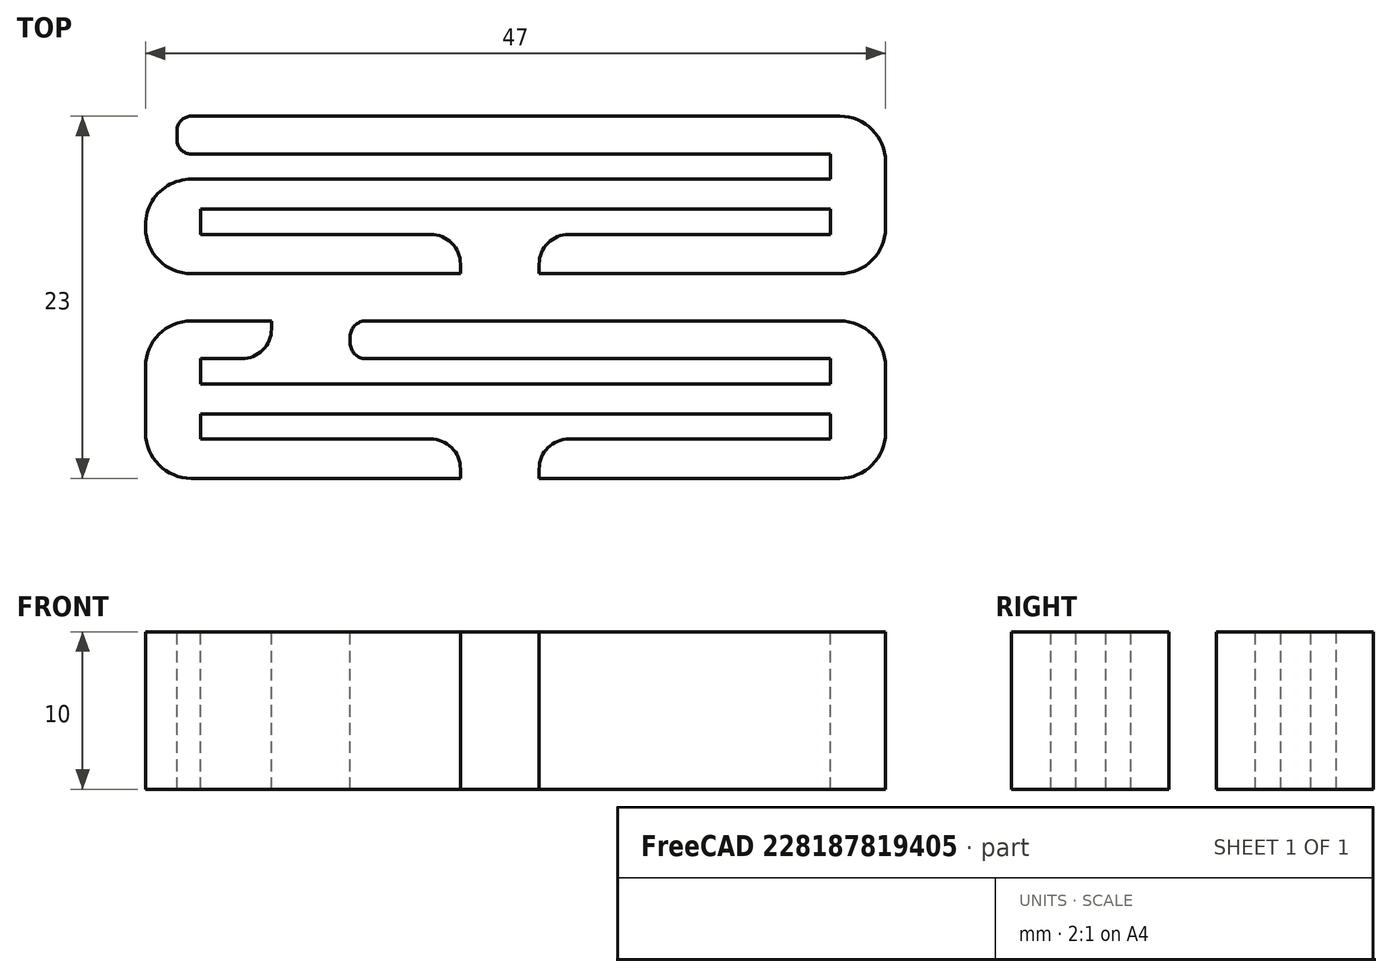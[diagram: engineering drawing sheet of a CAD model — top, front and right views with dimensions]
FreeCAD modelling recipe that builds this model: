
FCSTD DOCUMENT  (FreeCAD 0.16R6706 (Git))
Label: clip_mochila_40mm
License: CC-BY 3.0
LicenseURL: http://creativecommons.org/licenses/by/3.0/
objects: Part::Box×10, Part::Cut×8, Part::Fillet×7
note: 25 computed .brp shape members not serialized (recipe doc carries the construction recipe); baked Part::Feature solids carry a one-line shape summary decoded from their .brp

FEATURE [Part::Box] Box001  label="ext"
  Height = 10
  Length = 47
  Placement = pos=(-2,0,0) rot=(0,0,1;0rad)
  Width = 10
FEATURE [Part::Box] Box002  label="Cubo002"
  Height = 10
  Length = 40
  Placement = pos=(1.5,6,0) rot=(0,0,1;0rad)
  Width = 1.6
FEATURE [Part::Box] Box  label="Cubo003"
  Height = 10
  Length = 40
  Placement = pos=(1.5,2.5,0) rot=(0,0,1;0rad)
  Width = 1.6
FEATURE [Part::Box] Box003  label="Cubo004"
  Height = 10
  Length = 5
  Placement = pos=(18,0,0) rot=(0,0,1;0rad)
  Width = 2.5
FEATURE [Part::Box] Box004  label="Cubo005"
  Height = 10
  Length = 5
  Placement = pos=(6,6,0) rot=(0,0,1;0rad)
  Width = 4
FEATURE [Part::Cut] Cut
  Base = -> Box001
  Tool = -> Box004
FEATURE [Part::Cut] Cut001
  Base = -> Cut
  Tool = -> Box002
FEATURE [Part::Cut] Cut002
  Base = -> Cut001
  Tool = -> Box
FEATURE [Part::Cut] Cut003
  Base = -> Cut002
  Tool = -> Box003
FEATURE [Part::Fillet] Fillet
  Base = -> Cut003
  Edges = 4 edges r=2.9: [Edge1,Edge3,Edge59,Edge60]
FEATURE [Part::Fillet] Fillet001
  Base = -> Fillet
  Edges = 2 edges r=1: [Edge70,Edge72]
FEATURE [Part::Fillet] Fillet002
  Base = -> Fillet001
  Edges = 1 edges r=1.9: [Edge55]
FEATURE [Part::Fillet] Fillet003  label="Pechado"
  Base = -> Fillet002
  Edges = 2 edges r=1.9: [Edge62,Edge82]
FEATURE [Part::Box] Box005  label="ext001"
  Height = 10
  Length = 47
  Placement = pos=(-2,13,0) rot=(0,0,1;0rad)
  Width = 10
FEATURE [Part::Box] Box006  label="Cubo006"
  Height = 10
  Length = 43
  Placement = pos=(-1.5,19,0) rot=(0,0,1;0rad)
  Width = 1.6
FEATURE [Part::Box] Box007  label="Cubo007"
  Height = 10
  Length = 40
  Placement = pos=(1.5,15.5,0) rot=(0,0,1;0rad)
  Width = 1.6
FEATURE [Part::Box] Box008  label="Cubo008"
  Height = 10
  Length = 5
  Placement = pos=(18,13,0) rot=(0,0,1;0rad)
  Width = 2.5
FEATURE [Part::Box] Box009  label="Cubo009"
  Height = 10
  Length = 2
  Placement = pos=(-2,19,0) rot=(0,0,1;0rad)
  Width = 4
FEATURE [Part::Cut] Cut004
  Base = -> Box005
  Tool = -> Box006
FEATURE [Part::Cut] Cut005
  Base = -> Cut004
  Tool = -> Box007
FEATURE [Part::Cut] Cut006
  Base = -> Cut005
  Tool = -> Box008
FEATURE [Part::Cut] Cut007
  Base = -> Cut006
  Tool = -> Box009
FEATURE [Part::Fillet] Fillet004
  Base = -> Cut007
  Edges = 4 edges r=2.9: [Edge2,Edge4,Edge41,Edge43]
FEATURE [Part::Fillet] Fillet005
  Base = -> Fillet004
  Edges = 2 edges r=0.9: [Edge46,Edge48]
FEATURE [Part::Fillet] Fillet006  label="Aberto"
  Base = -> Fillet005
  Edges = 2 edges r=1.9: [Edge45,Edge65]
